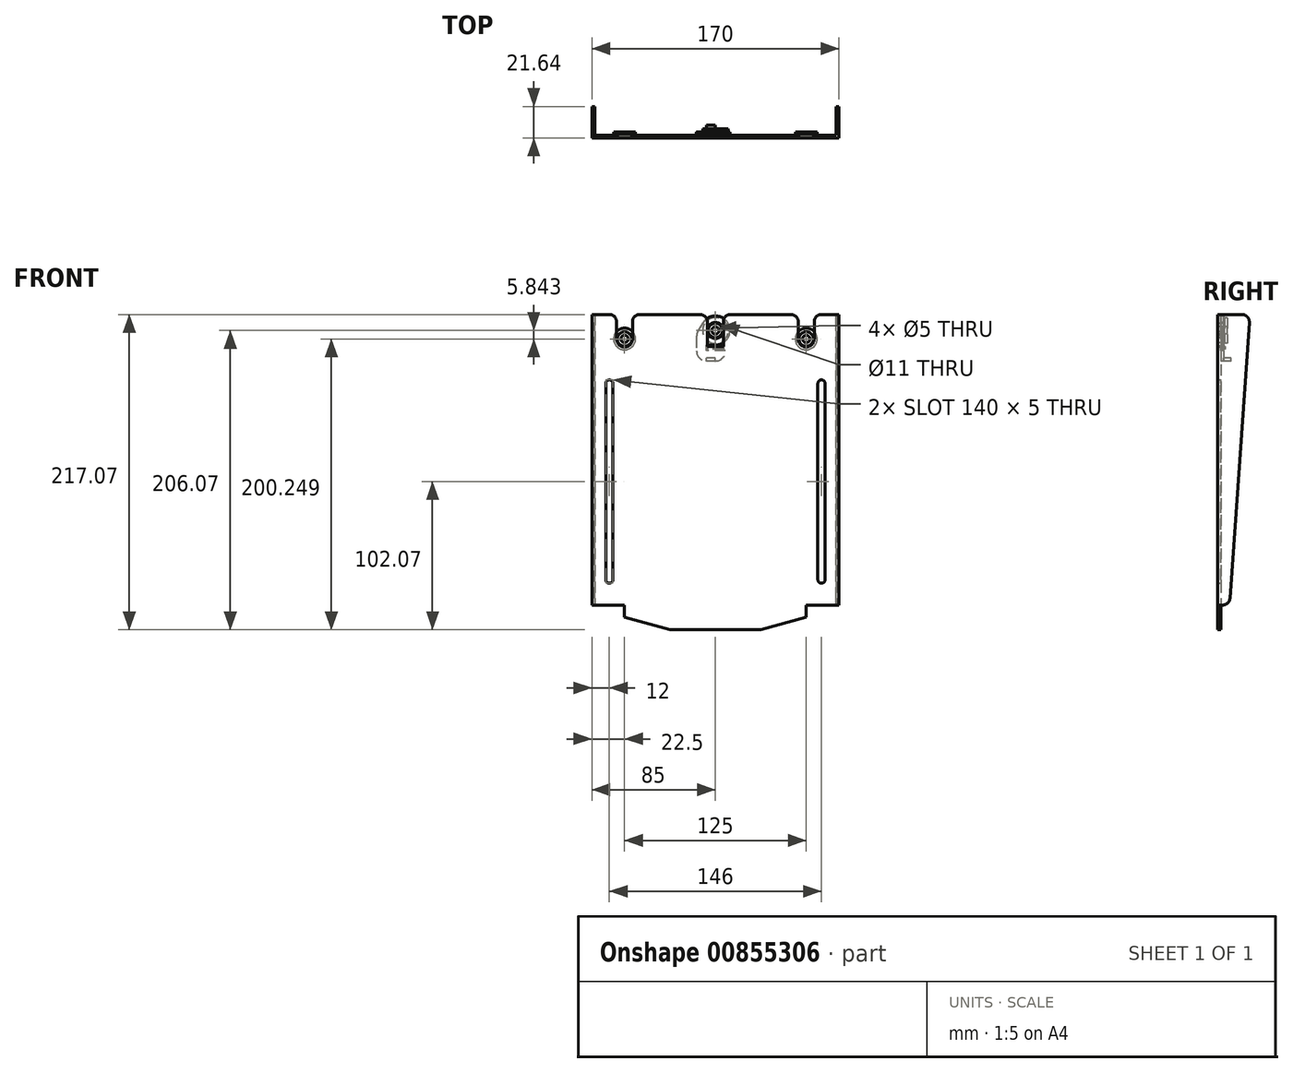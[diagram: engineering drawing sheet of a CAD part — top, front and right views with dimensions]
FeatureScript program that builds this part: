
annotation { "Feature Type Name" : "Feature", "Feature Type Description" : "" }
export const myFeature = defineFeature(function(context is Context, id is Id, definition is map)
    precondition{}
    {
        {
            var Q0;
            Q0=qCreatedBy(makeId("Front.planeOp"),FACE);
            var sketch = newSketch(context, id + "F0", { "sketchPlane" : qUnion([Q0])});
            skLineSegment(sketch, "E0.top", {"start": v(0, -100) * mm, "end": v(85, -100) * mm});
            skLineSegment(sketch, "E0.left", {"start": v(0, 100) * mm, "end": v(0, -100) * mm});
            skLineSegment(sketch, "E0.right", {"start": v(85, 100) * mm, "end": v(85, -100) * mm});
            skPoint(sketch, "E0.middle", {"position": v(42.5, 0) * mm});
            skLineSegment(sketch, "E1.left", {"start": v(0, 100) * mm, "end": v(0, 105) * mm});
            skLineSegment(sketch, "E2.MirrorCS", {"start": v(-85, 100) * mm, "end": v(-85, -100) * mm});
            skLineSegment(sketch, "E3.MirrorCS", {"start": v(0, -100) * mm, "end": v(-85, -100) * mm});
            skPoint(sketch, "E4.MirrorP", {"position": v(-42.5, 0) * mm});
            skLineSegment(sketch, "E5.bottom", {"start": v(73, -85) * mm, "end": v(73, -85) * mm});
            skLineSegment(sketch, "E5.top", {"start": v(73, 55) * mm, "end": v(73, 55) * mm});
            skLineSegment(sketch, "E5.left", {"start": v(70.5, -82.5) * mm, "end": v(70.5, 52.5) * mm});
            skLineSegment(sketch, "E5.right", {"start": v(75.5, -82.5) * mm, "end": v(75.5, 52.5) * mm});
            skPoint(sketch, "E5.middle", {"position": v(73, -15) * mm});
            skPoint(sketch, "E6.visualSharp", {"position": v(70.5, -85) * mm});
            skArc(sketch, "E6.filletArc", {"start": v(70.5, -82.5) * mm, "mid": v(71.23, -84.27) * mm, "end": v(73, -85) * mm});
            skPoint(sketch, "E7.visualSharp", {"position": v(75.5, -85) * mm});
            skArc(sketch, "E7.filletArc", {"start": v(73, -85) * mm, "mid": v(74.77, -84.27) * mm, "end": v(75.5, -82.5) * mm});
            skPoint(sketch, "E8.visualSharp", {"position": v(70.5, 55) * mm});
            skArc(sketch, "E8.filletArc", {"start": v(73, 55) * mm, "mid": v(71.23, 54.27) * mm, "end": v(70.5, 52.5) * mm});
            skPoint(sketch, "E9.visualSharp", {"position": v(75.5, 55) * mm});
            skArc(sketch, "E9.filletArc", {"start": v(75.5, 52.5) * mm, "mid": v(74.77, 54.27) * mm, "end": v(73, 55) * mm});
            skArc(sketch, "E10.MirrorCS", {"start": v(-70.5, -82.5) * mm, "mid": v(-71.23, -84.27) * mm, "end": v(-73, -85) * mm});
            skArc(sketch, "E11.MirrorCS", {"start": v(-75.5, 52.5) * mm, "mid": v(-74.77, 54.27) * mm, "end": v(-73, 55) * mm});
            skArc(sketch, "E12.MirrorCS", {"start": v(-73, -85) * mm, "mid": v(-74.77, -84.27) * mm, "end": v(-75.5, -82.5) * mm});
            skArc(sketch, "E13.MirrorCS", {"start": v(-73, 55) * mm, "mid": v(-71.23, 54.27) * mm, "end": v(-70.5, 52.5) * mm});
            skLineSegment(sketch, "E14.MirrorCS", {"start": v(-70.5, -82.5) * mm, "end": v(-70.5, 52.5) * mm});
            skLineSegment(sketch, "E15.MirrorCS", {"start": v(-75.5, -82.5) * mm, "end": v(-75.5, 52.5) * mm});
            skPoint(sketch, "E16.MirrorP", {"position": v(-70.5, -85) * mm});
            skPoint(sketch, "E17.MirrorP", {"position": v(-75.5, -85) * mm});
            skPoint(sketch, "E18.MirrorP", {"position": v(-75.5, 55) * mm});
            skPoint(sketch, "E19.MirrorP", {"position": v(-73, -15) * mm});
            skPoint(sketch, "E20.MirrorP", {"position": v(-70.5, 55) * mm});
            skLineSegment(sketch, "E21.MirrorCS", {"start": v(-73, -85) * mm, "end": v(-73, -85) * mm});
            skLineSegment(sketch, "E22.MirrorCS", {"start": v(-73, 55) * mm, "end": v(-73, 55) * mm});
            skLineSegment(sketch, "E23", {"start": v(0, -100) * mm, "end": v(0, -117.07) * mm});
            skLineSegment(sketch, "E24", {"start": v(0, -117.07) * mm, "end": v(-31.25, -117.07) * mm});
            skLineSegment(sketch, "E25", {"start": v(-62.5, -100) * mm, "end": v(-62.5, -108.5) * mm});
            skLineSegment(sketch, "E26", {"start": v(-62.5, -108.5) * mm, "end": v(-31.25, -117.07) * mm});
            skLineSegment(sketch, "E27.MirrorCS", {"start": v(62.5, -100) * mm, "end": v(62.5, -108.5) * mm});
            skLineSegment(sketch, "E28.MirrorCS", {"start": v(0, -117.07) * mm, "end": v(31.25, -117.07) * mm});
            skLineSegment(sketch, "E29.MirrorCS", {"start": v(62.5, -108.5) * mm, "end": v(31.25, -117.07) * mm});
            skLineSegment(sketch, "E30", {"start": v(-85, 100) * mm, "end": v(-73, 100) * mm});
            skLineSegment(sketch, "E31", {"start": v(-68, 95) * mm, "end": v(-68, 83.18) * mm});
            skLineSegment(sketch, "E32", {"start": v(-62.5, 77.68) * mm, "end": v(-62.5, 77.68) * mm});
            skLineSegment(sketch, "E33", {"start": v(-57, 83.18) * mm, "end": v(-57, 95) * mm});
            skPoint(sketch, "E34.visualSharp", {"position": v(-68, 77.68) * mm});
            skArc(sketch, "E34.filletArc", {"start": v(-68, 83.18) * mm, "mid": v(-66.39, 79.29) * mm, "end": v(-62.5, 77.68) * mm});
            skPoint(sketch, "E35.visualSharp", {"position": v(-57, 77.68) * mm});
            skArc(sketch, "E35.filletArc", {"start": v(-62.5, 77.68) * mm, "mid": v(-58.61, 79.29) * mm, "end": v(-57, 83.18) * mm});
            skLineSegment(sketch, "E36.MirrorCS", {"start": v(57, 83.18) * mm, "end": v(57, 95) * mm});
            skPoint(sketch, "E37.MirrorP", {"position": v(57, 77.68) * mm});
            skArc(sketch, "E38.MirrorCS", {"start": v(62.5, 77.68) * mm, "mid": v(58.61, 79.29) * mm, "end": v(57, 83.18) * mm});
            skArc(sketch, "E39.MirrorCS", {"start": v(68, 83.18) * mm, "mid": v(66.39, 79.29) * mm, "end": v(62.5, 77.68) * mm});
            skLineSegment(sketch, "E40.MirrorCS", {"start": v(68, 95) * mm, "end": v(68, 83.18) * mm});
            skLineSegment(sketch, "E41.MirrorCS", {"start": v(85, 100) * mm, "end": v(73, 100) * mm});
            skPoint(sketch, "E42.visualSharp", {"position": v(57, 100) * mm});
            skArc(sketch, "E42.filletArc", {"start": v(57, 95) * mm, "mid": v(55.54, 98.54) * mm, "end": v(52, 100) * mm});
            skPoint(sketch, "E43.visualSharp", {"position": v(68, 100) * mm});
            skArc(sketch, "E43.filletArc", {"start": v(73, 100) * mm, "mid": v(69.46, 98.54) * mm, "end": v(68, 95) * mm});
            skPoint(sketch, "E44.visualSharp", {"position": v(-57, 100) * mm});
            skArc(sketch, "E44.filletArc", {"start": v(-52, 100) * mm, "mid": v(-55.54, 98.54) * mm, "end": v(-57, 95) * mm});
            skPoint(sketch, "E45.visualSharp", {"position": v(-68, 100) * mm});
            skArc(sketch, "E45.filletArc", {"start": v(-68, 95) * mm, "mid": v(-69.46, 98.54) * mm, "end": v(-73, 100) * mm});
            skLineSegment(sketch, "E46", {"start": v(5.5, 95) * mm, "end": v(5.5, 78) * mm});
            skLineSegment(sketch, "E47", {"start": v(5.5, 78) * mm, "end": v(-5.5, 78) * mm});
            skLineSegment(sketch, "E48", {"start": v(-5.5, 78) * mm, "end": v(-5.5, 95) * mm});
            skLineSegment(sketch, "E49", {"start": v(52, 100) * mm, "end": v(10.5, 100) * mm});
            skLineSegment(sketch, "E50", {"start": v(-52, 100) * mm, "end": v(-10.5, 100) * mm});
            skPoint(sketch, "E51.visualSharp", {"position": v(-5.5, 100) * mm});
            skArc(sketch, "E51.filletArc", {"start": v(-5.5, 95) * mm, "mid": v(-6.96, 98.54) * mm, "end": v(-10.5, 100) * mm});
            skPoint(sketch, "E52.visualSharp", {"position": v(5.5, 100) * mm});
            skArc(sketch, "E52.filletArc", {"start": v(10.5, 100) * mm, "mid": v(6.96, 98.54) * mm, "end": v(5.5, 95) * mm});
            skSolve(sketch);
        }
        {
            var Q0;
            Q0 = qSketchRegion(id + "F0", true);
            extrude(context, id + "F1", {"entities" : qUnion([Q0]), "depth" : 2 * mm, "offsetDistance" : 25 * mm});
        }
        {
            var Q0;
            Q0=makeQuery(id+"F1.opExtrude","CAP_FACE",FACE,{"disambiguationData":[OSD([sQuery(id+"F0.wireOp",EDGE,"E0.bottom"),sQuery(id+"F0.wireOp",EDGE,"E0.top"),sQuery(id+"F0.wireOp",EDGE,"E0.right"),sQuery(id+"F0.wireOp",EDGE,"frcyEhX3-ksV9-Io33-VOOh-hWverEK9uXBL.left"),sQuery(id+"F0.wireOp",EDGE,"frcyEhX3-ksV9-Io33-VOOh-hWverEK9uXBL.right"),sQuery(id+"F0.wireOp",EDGE,"ycnwuAfa-UpH9-AvOl-Gm3H-XGRiDgKgmbUQ"),sQuery(id+"F0.wireOp",EDGE,"YSR243FN-PfGp-wJLQ-lxfN-2wXKMQRAt0pg"),sQuery(id+"F0.wireOp",EDGE,"E1.bottom"),sQuery(id+"F0.wireOp",EDGE,"f4791902-98f6-4560-8930-070e0529dc460.MirrorCS"),sQuery(id+"F0.wireOp",EDGE,"f4791902-98f6-4560-8930-070e0529dc461.MirrorCS"),sQuery(id+"F0.wireOp",EDGE,"E2.MirrorCS"),sQuery(id+"F0.wireOp",EDGE,"f4791902-98f6-4560-8930-070e0529dc4612.MirrorCS"),sQuery(id+"F0.wireOp",EDGE,"f4791902-98f6-4560-8930-070e0529dc4615.MirrorCS"),sQuery(id+"F0.wireOp",EDGE,"E3.MirrorCS"),sQuery(id+"F0.wireOp",EDGE,"f4791902-98f6-4560-8930-070e0529dc4617.MirrorCS"),sQuery(id+"F0.wireOp",EDGE,"f4791902-98f6-4560-8930-070e0529dc4623.MirrorCS")])],"isStart":true});
            var sketch = newSketch(context, id + "F2", { "sketchPlane" : qUnion([Q0])});
            skArc(sketch, "E53", {"start": v(-10, 89) * mm, "mid": v(-7.07, 81.93) * mm, "end": v(0, 79) * mm});
            skCircle(sketch, "E54", {"center": v(0, 89) * mm, "radius": 5.5 * mm});
            skLineSegment(sketch, "E55", {"start": v(0, 79) * mm, "end": v(6, 79) * mm});
            skLineSegment(sketch, "E56", {"start": v(-7, 75) * mm, "end": v(6, 75) * mm});
            skLineSegment(sketch, "E57", {"start": v(6, 75) * mm, "end": v(6, 79) * mm});
            skArc(sketch, "E58", {"start": v(-7, 75) * mm, "mid": v(-4.95, 70.05) * mm, "end": v(0, 68) * mm});
            skLineSegment(sketch, "E59", {"start": v(13, 84.44) * mm, "end": v(13, 75) * mm});
            skLineSegment(sketch, "E60", {"start": v(0, 68) * mm, "end": v(6, 68) * mm});
            skPoint(sketch, "E61.visualSharp", {"position": v(13, 68) * mm});
            skArc(sketch, "E61.filletArc", {"start": v(6, 68) * mm, "mid": v(10.95, 70.05) * mm, "end": v(13, 75) * mm});
            skPoint(sketch, "E62.visualSharp", {"position": v(13, 89) * mm});
            skLineSegment(sketch, "E63", {"start": v(11.65, 89.18) * mm, "end": v(8.5, 94.26) * mm});
            skArc(sketch, "E64", {"start": v(0, 79) * mm, "mid": v(-8.74, 93.87) * mm, "end": v(8.5, 94.26) * mm});
            skPoint(sketch, "E65.visualSharp", {"position": v(13, 87) * mm});
            skArc(sketch, "E65.filletArc", {"start": v(13, 84.44) * mm, "mid": v(12.66, 86.9) * mm, "end": v(11.65, 89.18) * mm});
            skSolve(sketch);
        }
        {
            var Q0;
            Q0 = qSketchRegion(id + "F2", true);
            extrude(context, id + "F3", {"entities" : qUnion([Q0]), "depth" : 2 * mm, "offsetDistance" : 25 * mm});
        }
        {
            var Q0;
            Q0=makeQuery(id+"F1.opExtrude","SWEPT_FACE",FACE,{"disambiguationData":[OSD([sQuery(id+"F0.wireOp",EDGE,"E2.MirrorCS")])]});
            var sketch = newSketch(context, id + "F4", { "sketchPlane" : qUnion([Q0])});
            skLineSegment(sketch, "E66", {"start": v(0, 100) * mm, "end": v(-14.64, 100) * mm});
            skLineSegment(sketch, "E67", {"start": v(0, -100) * mm, "end": v(-1.34, -100) * mm});
            skLineSegment(sketch, "E68", {"start": v(-6.33, -95.35) * mm, "end": v(-19.63, 94.65) * mm});
            skLineSegment(sketch, "E69", {"start": v(0, 100) * mm, "end": v(0, -100) * mm});
            skPoint(sketch, "E70.visualSharp", {"position": v(-20, 100) * mm});
            skArc(sketch, "E70.filletArc", {"start": v(-14.64, 100) * mm, "mid": v(-18.3, 98.4) * mm, "end": v(-19.63, 94.65) * mm});
            skPoint(sketch, "E71.visualSharp", {"position": v(-6, -100) * mm});
            skArc(sketch, "E71.filletArc", {"start": v(-6.33, -95.35) * mm, "mid": v(-4.75, -98.66) * mm, "end": v(-1.34, -100) * mm});
            skSolve(sketch);
        }
        {
            var Q0;
            Q0 = qSketchRegion(id + "F4", true);
            extrude(context, id + "F5", {"entities" : qUnion([Q0]), "oppositeDirection" : true, "depth" : 2 * mm, "offsetDistance" : 25 * mm});
        }
        {
            var Q0;
            Q0=makeQuery(id+"F1.opExtrude","SWEPT_FACE",FACE,{"disambiguationData":[OSD([sQuery(id+"F0.wireOp",EDGE,"E0.right")])]});
            var sketch = newSketch(context, id + "F6", { "sketchPlane" : qUnion([Q0])});
            skLineSegment(sketch, "E72", {"start": v(0, 100) * mm, "end": v(14.64, 100) * mm});
            skLineSegment(sketch, "E73", {"start": v(0, -100) * mm, "end": v(1.34, -100) * mm});
            skLineSegment(sketch, "E74", {"start": v(6.33, -95.35) * mm, "end": v(19.63, 94.65) * mm});
            skLineSegment(sketch, "E75", {"start": v(0, 100) * mm, "end": v(0, -100) * mm});
            skPoint(sketch, "E76.visualSharp", {"position": v(6, -100) * mm});
            skArc(sketch, "E76.filletArc", {"start": v(1.34, -100) * mm, "mid": v(4.75, -98.66) * mm, "end": v(6.33, -95.35) * mm});
            skPoint(sketch, "E77.visualSharp", {"position": v(20, 100) * mm});
            skArc(sketch, "E77.filletArc", {"start": v(19.63, 94.65) * mm, "mid": v(18.3, 98.4) * mm, "end": v(14.64, 100) * mm});
            skSolve(sketch);
        }
        {
            var Q0;
            Q0 = qSketchRegion(id + "F6", true);
            extrude(context, id + "F7", {"entities" : qUnion([Q0]), "operationType" : NewBodyOperationType.ADD, "oppositeDirection" : true, "depth" : 2 * mm, "offsetDistance" : 25 * mm});
        }
        {
            var Q0;
            Q0=qCreatedBy(makeId("Front.planeOp"),FACE);
            var sketch = newSketch(context, id + "F8", { "sketchPlane" : qUnion([Q0])});
            skLineSegment(sketch, "E78.bottom", {"start": v(5.5, 78) * mm, "end": v(-5.46, 78) * mm});
            skLineSegment(sketch, "E78.top", {"start": v(5.5, 76.07) * mm, "end": v(-5.46, 76.07) * mm});
            skLineSegment(sketch, "E78.left", {"start": v(5.5, 78) * mm, "end": v(5.5, 76.07) * mm});
            skLineSegment(sketch, "E78.right", {"start": v(-5.46, 78) * mm, "end": v(-5.46, 76.07) * mm});
            skSolve(sketch);
        }
        {
            var Q0;
            Q0 = qSketchRegion(id + "F8", true);
            extrude(context, id + "F9", {"entities" : qUnion([Q0]), "operationType" : NewBodyOperationType.ADD, "oppositeDirection" : true, "depth" : 3 * mm, "offsetDistance" : 25 * mm});
        }
        {
            var Q0;
            Q0=makeQuery(id+"F1.opExtrude","CAP_FACE",FACE,{"disambiguationData":[OSD([sQuery(id+"F0.wireOp",EDGE,"E0.right"),sQuery(id+"F0.wireOp",EDGE,"E2.MirrorCS"),sQuery(id+"F0.wireOp",EDGE,"E5.left"),sQuery(id+"F0.wireOp",EDGE,"E5.right"),sQuery(id+"F0.wireOp",EDGE,"E6.filletArc"),sQuery(id+"F0.wireOp",EDGE,"E7.filletArc"),sQuery(id+"F0.wireOp",EDGE,"E8.filletArc"),sQuery(id+"F0.wireOp",EDGE,"E9.filletArc"),sQuery(id+"F0.wireOp",EDGE,"E10.MirrorCS"),sQuery(id+"F0.wireOp",EDGE,"E13.MirrorCS"),sQuery(id+"F0.wireOp",EDGE,"E12.MirrorCS"),sQuery(id+"F0.wireOp",EDGE,"E11.MirrorCS"),sQuery(id+"F0.wireOp",EDGE,"E14.MirrorCS"),sQuery(id+"F0.wireOp",EDGE,"E15.MirrorCS"),sQuery(id+"F0.wireOp",EDGE,"E24"),sQuery(id+"F0.wireOp",EDGE,"E25"),sQuery(id+"F0.wireOp",EDGE,"E26"),sQuery(id+"F0.wireOp",EDGE,"E27.MirrorCS"),sQuery(id+"F0.wireOp",EDGE,"E28.MirrorCS"),sQuery(id+"F0.wireOp",EDGE,"E29.MirrorCS"),sQuery(id+"F0.wireOp",EDGE,"E3.MirrorCS"),sQuery(id+"F0.wireOp",EDGE,"E0.top"),sQuery(id+"F0.wireOp",EDGE,"E30"),sQuery(id+"F0.wireOp",EDGE,"E31"),sQuery(id+"F0.wireOp",EDGE,"E33"),sQuery(id+"F0.wireOp",EDGE,"E34.filletArc"),sQuery(id+"F0.wireOp",EDGE,"E35.filletArc"),sQuery(id+"F0.wireOp",EDGE,"E36.MirrorCS"),sQuery(id+"F0.wireOp",EDGE,"E38.MirrorCS"),sQuery(id+"F0.wireOp",EDGE,"E39.MirrorCS"),sQuery(id+"F0.wireOp",EDGE,"E40.MirrorCS"),sQuery(id+"F0.wireOp",EDGE,"E41.MirrorCS"),sQuery(id+"F0.wireOp",EDGE,"E42.filletArc"),sQuery(id+"F0.wireOp",EDGE,"E43.filletArc"),sQuery(id+"F0.wireOp",EDGE,"E44.filletArc"),sQuery(id+"F0.wireOp",EDGE,"E45.filletArc"),sQuery(id+"F0.wireOp",EDGE,"E46"),sQuery(id+"F0.wireOp",EDGE,"E47"),sQuery(id+"F0.wireOp",EDGE,"E48"),sQuery(id+"F0.wireOp",EDGE,"E49"),sQuery(id+"F0.wireOp",EDGE,"E50"),sQuery(id+"F0.wireOp",EDGE,"E51.filletArc"),sQuery(id+"F0.wireOp",EDGE,"E52.filletArc")])],"isStart":false});
            var sketch = newSketch(context, id + "F10", { "sketchPlane" : qUnion([Q0])});
            skCircle(sketch, "E79", {"center": v(0, 89.02) * mm, "radius": 5 * mm});
            skCircle(sketch, "E80", {"center": v(0, 89.02) * mm, "radius": 2.5 * mm});
            skSolve(sketch);
        }
        {
            var Q0;
            Q0 = qSketchRegion(id + "F10", true);
            extrude(context, id + "F11", {"entities" : qUnion([Q0]), "oppositeDirection" : true, "depth" : 4.5 * mm, "offsetDistance" : 25 * mm});
        }
        {
            var Q0;
            Q0=makeQuery(id+"F11.opExtrude","CAP_FACE",FACE,{"disambiguationData":[OSD([sQuery(id+"F10.wireOp",EDGE,"E79"),sQuery(id+"F10.wireOp",EDGE,"E80")])],"isStart":false});
            var sketch = newSketch(context, id + "F12", { "sketchPlane" : qUnion([Q0])});
            skCircle(sketch, "E81", {"center": v(0, 89.02) * mm, "radius": 2.5 * mm});
            skCircle(sketch, "E82", {"center": v(0, 89.02) * mm, "radius": 8.84 * mm});
            skSolve(sketch);
        }
        {
            var Q0;
            Q0 = qSketchRegion(id + "F12", true);
            extrude(context, id + "F13", {"entities" : qUnion([Q0]), "depth" : 2 * mm, "offsetDistance" : 25 * mm});
        }
        {
            var Q0;
            Q0=makeQuery(id+"F3.opExtrude","CAP_FACE",FACE,{"disambiguationData":[OSD([sQuery(id+"F2.wireOp",EDGE,"E54"),sQuery(id+"F2.wireOp",EDGE,"E55"),sQuery(id+"F2.wireOp",EDGE,"E56"),sQuery(id+"F2.wireOp",EDGE,"E57"),sQuery(id+"F2.wireOp",EDGE,"E58"),sQuery(id+"F2.wireOp",EDGE,"E59"),sQuery(id+"F2.wireOp",EDGE,"E60"),sQuery(id+"F2.wireOp",EDGE,"E61.filletArc"),sQuery(id+"F2.wireOp",EDGE,"E63"),sQuery(id+"F2.wireOp",EDGE,"E64"),sQuery(id+"F2.wireOp",EDGE,"E65.filletArc")])],"isStart":false});
            var sketch = newSketch(context, id + "F14", { "sketchPlane" : qUnion([Q0])});
            skLineSegment(sketch, "E83.bottom", {"start": v(0, 68) * mm, "end": v(6, 68) * mm});
            skLineSegment(sketch, "E83.top", {"start": v(0, 70) * mm, "end": v(6, 70) * mm});
            skLineSegment(sketch, "E83.left", {"start": v(0, 68) * mm, "end": v(0, 70) * mm});
            skLineSegment(sketch, "E83.right", {"start": v(6, 68) * mm, "end": v(6, 70) * mm});
            skSolve(sketch);
        }
        {
            var Q0;
            Q0 = qSketchRegion(id + "F14", true);
            extrude(context, id + "F15", {"entities" : qUnion([Q0]), "operationType" : NewBodyOperationType.ADD, "depth" : 5 * mm, "offsetDistance" : 25 * mm});
        }
        {
            var Q0;
            Q0=makeQuery(id+"F1.opExtrude","CAP_FACE",FACE,{"disambiguationData":[OSD([sQuery(id+"F0.wireOp",EDGE,"E0.right"),sQuery(id+"F0.wireOp",EDGE,"E2.MirrorCS"),sQuery(id+"F0.wireOp",EDGE,"E5.left"),sQuery(id+"F0.wireOp",EDGE,"E5.right"),sQuery(id+"F0.wireOp",EDGE,"E6.filletArc"),sQuery(id+"F0.wireOp",EDGE,"E7.filletArc"),sQuery(id+"F0.wireOp",EDGE,"E8.filletArc"),sQuery(id+"F0.wireOp",EDGE,"E9.filletArc"),sQuery(id+"F0.wireOp",EDGE,"E10.MirrorCS"),sQuery(id+"F0.wireOp",EDGE,"E13.MirrorCS"),sQuery(id+"F0.wireOp",EDGE,"E12.MirrorCS"),sQuery(id+"F0.wireOp",EDGE,"E11.MirrorCS"),sQuery(id+"F0.wireOp",EDGE,"E14.MirrorCS"),sQuery(id+"F0.wireOp",EDGE,"E15.MirrorCS"),sQuery(id+"F0.wireOp",EDGE,"E24"),sQuery(id+"F0.wireOp",EDGE,"E25"),sQuery(id+"F0.wireOp",EDGE,"E26"),sQuery(id+"F0.wireOp",EDGE,"E27.MirrorCS"),sQuery(id+"F0.wireOp",EDGE,"E28.MirrorCS"),sQuery(id+"F0.wireOp",EDGE,"E29.MirrorCS"),sQuery(id+"F0.wireOp",EDGE,"E3.MirrorCS"),sQuery(id+"F0.wireOp",EDGE,"E0.top"),sQuery(id+"F0.wireOp",EDGE,"E30"),sQuery(id+"F0.wireOp",EDGE,"E31"),sQuery(id+"F0.wireOp",EDGE,"E33"),sQuery(id+"F0.wireOp",EDGE,"E34.filletArc"),sQuery(id+"F0.wireOp",EDGE,"E35.filletArc"),sQuery(id+"F0.wireOp",EDGE,"E36.MirrorCS"),sQuery(id+"F0.wireOp",EDGE,"E38.MirrorCS"),sQuery(id+"F0.wireOp",EDGE,"E39.MirrorCS"),sQuery(id+"F0.wireOp",EDGE,"E40.MirrorCS"),sQuery(id+"F0.wireOp",EDGE,"E41.MirrorCS"),sQuery(id+"F0.wireOp",EDGE,"E42.filletArc"),sQuery(id+"F0.wireOp",EDGE,"E43.filletArc"),sQuery(id+"F0.wireOp",EDGE,"E44.filletArc"),sQuery(id+"F0.wireOp",EDGE,"E45.filletArc"),sQuery(id+"F0.wireOp",EDGE,"E46"),sQuery(id+"F0.wireOp",EDGE,"E47"),sQuery(id+"F0.wireOp",EDGE,"E48"),sQuery(id+"F0.wireOp",EDGE,"E49"),sQuery(id+"F0.wireOp",EDGE,"E50"),sQuery(id+"F0.wireOp",EDGE,"E51.filletArc"),sQuery(id+"F0.wireOp",EDGE,"E52.filletArc")])],"isStart":false});
            var sketch = newSketch(context, id + "F16", { "sketchPlane" : qUnion([Q0])});
            skCircle(sketch, "E84", {"center": v(-62.5, 83.18) * mm, "radius": 5 * mm});
            skCircle(sketch, "E85", {"center": v(-62.5, 83.18) * mm, "radius": 2.5 * mm});
            skSolve(sketch);
        }
        {
            var Q0;
            Q0 = qSketchRegion(id + "F16", true);
            extrude(context, id + "F17", {"entities" : qUnion([Q0]), "oppositeDirection" : true, "depth" : 3 * mm, "offsetDistance" : 25 * mm});
        }
        {
            var Q0;
            Q0=makeQuery(id+"F17.opExtrude","CAP_FACE",FACE,{"disambiguationData":[OSD([sQuery(id+"F16.wireOp",EDGE,"E84"),sQuery(id+"F16.wireOp",EDGE,"E85")])],"isStart":false});
            var sketch = newSketch(context, id + "F18", { "sketchPlane" : qUnion([Q0])});
            skCircle(sketch, "E86", {"center": v(62.5, 83.18) * mm, "radius": 7.5 * mm});
            skCircle(sketch, "E87", {"center": v(62.5, 83.18) * mm, "radius": 2.5 * mm});
            skSolve(sketch);
        }
        {
            var Q0;
            Q0 = qSketchRegion(id + "F18", true);
            extrude(context, id + "F19", {"entities" : qUnion([Q0]), "operationType" : NewBodyOperationType.ADD, "depth" : 1 * mm, "offsetDistance" : 25 * mm});
        }
        {
            var Q0;
            Q0=makeQuery(id+"F1.opExtrude","CAP_FACE",FACE,{"disambiguationData":[OSD([sQuery(id+"F0.wireOp",EDGE,"E0.right"),sQuery(id+"F0.wireOp",EDGE,"E2.MirrorCS"),sQuery(id+"F0.wireOp",EDGE,"E5.left"),sQuery(id+"F0.wireOp",EDGE,"E5.right"),sQuery(id+"F0.wireOp",EDGE,"E6.filletArc"),sQuery(id+"F0.wireOp",EDGE,"E7.filletArc"),sQuery(id+"F0.wireOp",EDGE,"E8.filletArc"),sQuery(id+"F0.wireOp",EDGE,"E9.filletArc"),sQuery(id+"F0.wireOp",EDGE,"E10.MirrorCS"),sQuery(id+"F0.wireOp",EDGE,"E13.MirrorCS"),sQuery(id+"F0.wireOp",EDGE,"E12.MirrorCS"),sQuery(id+"F0.wireOp",EDGE,"E11.MirrorCS"),sQuery(id+"F0.wireOp",EDGE,"E14.MirrorCS"),sQuery(id+"F0.wireOp",EDGE,"E15.MirrorCS"),sQuery(id+"F0.wireOp",EDGE,"E24"),sQuery(id+"F0.wireOp",EDGE,"E25"),sQuery(id+"F0.wireOp",EDGE,"E26"),sQuery(id+"F0.wireOp",EDGE,"E27.MirrorCS"),sQuery(id+"F0.wireOp",EDGE,"E28.MirrorCS"),sQuery(id+"F0.wireOp",EDGE,"E29.MirrorCS"),sQuery(id+"F0.wireOp",EDGE,"E3.MirrorCS"),sQuery(id+"F0.wireOp",EDGE,"E0.top"),sQuery(id+"F0.wireOp",EDGE,"E30"),sQuery(id+"F0.wireOp",EDGE,"E31"),sQuery(id+"F0.wireOp",EDGE,"E33"),sQuery(id+"F0.wireOp",EDGE,"E34.filletArc"),sQuery(id+"F0.wireOp",EDGE,"E35.filletArc"),sQuery(id+"F0.wireOp",EDGE,"E36.MirrorCS"),sQuery(id+"F0.wireOp",EDGE,"E38.MirrorCS"),sQuery(id+"F0.wireOp",EDGE,"E39.MirrorCS"),sQuery(id+"F0.wireOp",EDGE,"E40.MirrorCS"),sQuery(id+"F0.wireOp",EDGE,"E41.MirrorCS"),sQuery(id+"F0.wireOp",EDGE,"E42.filletArc"),sQuery(id+"F0.wireOp",EDGE,"E43.filletArc"),sQuery(id+"F0.wireOp",EDGE,"E44.filletArc"),sQuery(id+"F0.wireOp",EDGE,"E45.filletArc"),sQuery(id+"F0.wireOp",EDGE,"E46"),sQuery(id+"F0.wireOp",EDGE,"E47"),sQuery(id+"F0.wireOp",EDGE,"E48"),sQuery(id+"F0.wireOp",EDGE,"E49"),sQuery(id+"F0.wireOp",EDGE,"E50"),sQuery(id+"F0.wireOp",EDGE,"E51.filletArc"),sQuery(id+"F0.wireOp",EDGE,"E52.filletArc")])],"isStart":false});
            var sketch = newSketch(context, id + "F20", { "sketchPlane" : qUnion([Q0])});
            skCircle(sketch, "E88", {"center": v(62.5, 83.18) * mm, "radius": 5 * mm});
            skCircle(sketch, "E89", {"center": v(62.5, 83.18) * mm, "radius": 2.5 * mm});
            skSolve(sketch);
        }
        {
            var Q0;
            Q0 = qSketchRegion(id + "F20", true);
            extrude(context, id + "F21", {"entities" : qUnion([Q0]), "oppositeDirection" : true, "depth" : 3 * mm, "offsetDistance" : 25 * mm});
        }
        {
            var Q0;
            Q0=makeQuery(id+"F21.opExtrude","CAP_FACE",FACE,{"disambiguationData":[OSD([sQuery(id+"F20.wireOp",EDGE,"E88"),sQuery(id+"F20.wireOp",EDGE,"E89")])],"isStart":false});
            var sketch = newSketch(context, id + "F22", { "sketchPlane" : qUnion([Q0])});
            skCircle(sketch, "E90", {"center": v(-62.5, 83.18) * mm, "radius": 7.5 * mm});
            skCircle(sketch, "E91", {"center": v(-62.5, 83.18) * mm, "radius": 2.5 * mm});
            skSolve(sketch);
        }
        {
            var Q0;
            Q0 = qSketchRegion(id + "F22", true);
            extrude(context, id + "F23", {"entities" : qUnion([Q0]), "operationType" : NewBodyOperationType.ADD, "depth" : 1 * mm, "offsetDistance" : 25 * mm});
        }
    });
